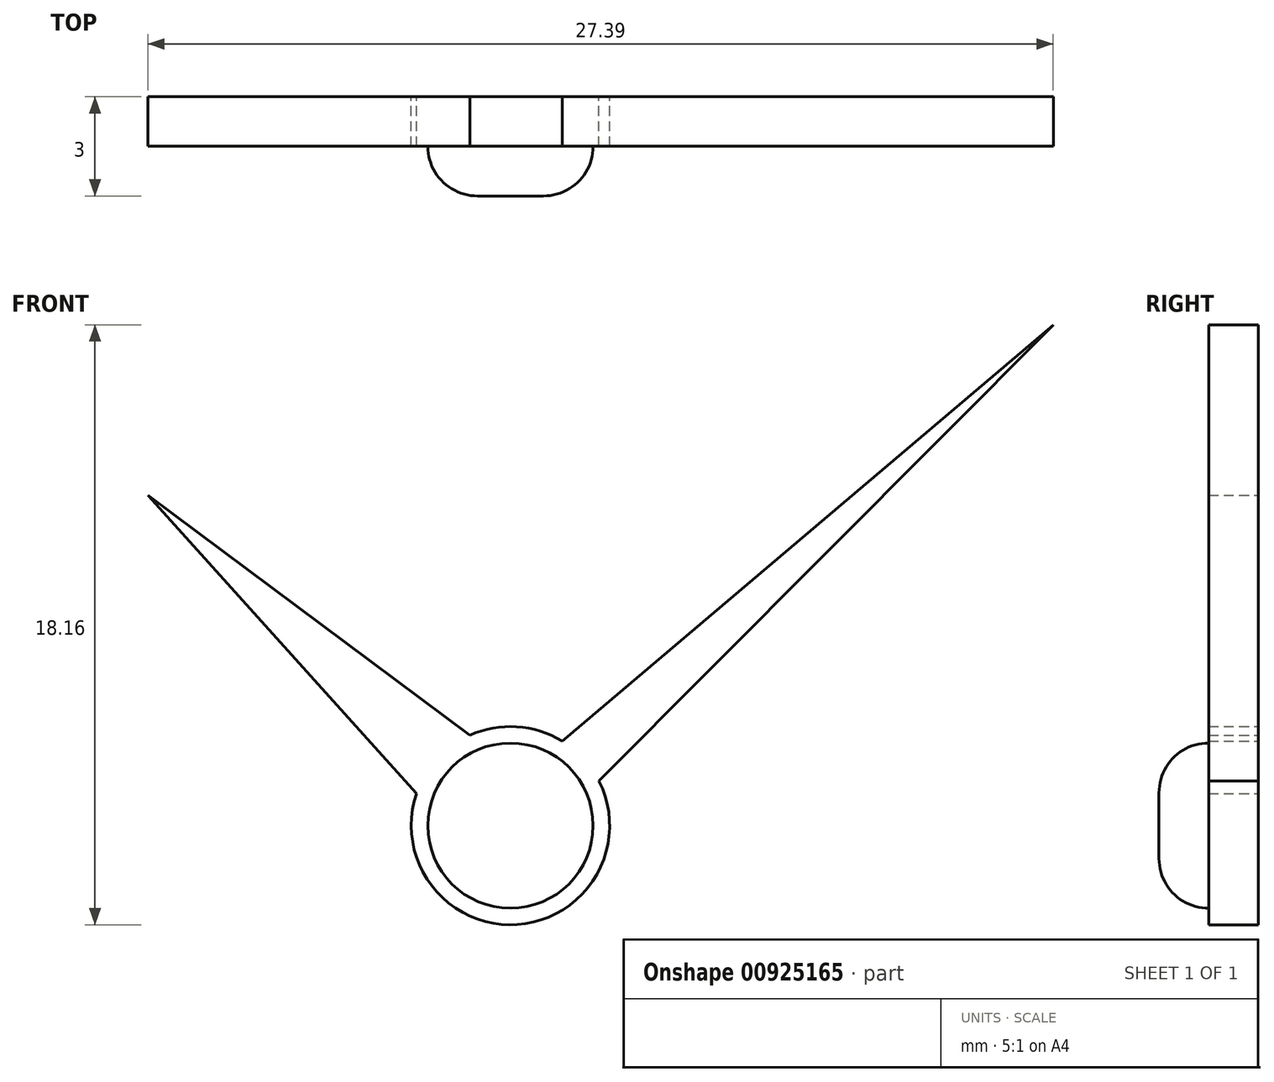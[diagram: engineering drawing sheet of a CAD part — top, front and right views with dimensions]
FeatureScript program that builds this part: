
annotation { "Feature Type Name" : "Feature", "Feature Type Description" : "" }
export const myFeature = defineFeature(function(context is Context, id is Id, definition is map)
    precondition{}
    {
        {
            var Q0;
            Q0=qCreatedBy(makeId("Front.planeOp"),FACE);
            var sketch = newSketch(context, id + "F0", { "sketchPlane" : qUnion([Q0])});
            skCircle(sketch, "E0", {"center": v(0, 0) * mm, "radius": 2.5 * mm});
            skSolve(sketch);
        }
        {
            var Q0;
            Q0 = qSketchRegion(id + "F0", true);
            extrude(context, id + "F1", {"entities" : qUnion([Q0]), "depth" : 3 * mm, "offsetDistance" : 25 * mm});
        }
        {
            var Q0;
            Q0=makeQuery(id+"F1.opExtrude","CAP_EDGE",EDGE,{"disambiguationData":[OSD([sQuery(id+"F0.wireOp",EDGE,"E0")])],"isStart":false});
            fillet(context, id + "F2", {"entities" : qUnion([Q0]), "radius" : 1.5 * mm, "tangentPropagation" : true, "allowEdgeOverflow" : false});
        }
        {
            var Q0;
            Q0=qCreatedBy(makeId("Front.planeOp"),FACE);
            var sketch = newSketch(context, id + "F3", { "sketchPlane" : qUnion([Q0])});
            skArc(sketch, "E1", {"start": v(-2.84, 0.97) * mm, "mid": v(0.2, -3) * mm, "end": v(2.68, 1.36) * mm});
            skLineSegment(sketch, "E2", {"start": v(0, 0) * mm, "end": v(22.1, 20.4) * mm, "construction": true});
            skLineSegment(sketch, "E3", {"start": v(0, 0) * mm, "end": v(-13.96, 12.72) * mm, "construction": true});
            skLineSegment(sketch, "E4", {"start": v(-10.97, 10) * mm, "end": v(-2.84, 0.97) * mm});
            skLineSegment(sketch, "E5.MirrorCS", {"start": v(-10.97, 10) * mm, "end": v(-1.23, 2.74) * mm});
            skLineSegment(sketch, "E6", {"start": v(1.57, 2.56) * mm, "end": v(16.42, 15.16) * mm});
            skLineSegment(sketch, "E7.MirrorCS", {"start": v(2.68, 1.36) * mm, "end": v(16.42, 15.16) * mm});
            skArc(sketch, "E8.trimOffspring", {"start": v(1.57, 2.56) * mm, "mid": v(0.19, 3) * mm, "end": v(-1.23, 2.74) * mm});
            skSolve(sketch);
        }
        {
            var Q0;
            Q0 = qSketchRegion(id + "F3", true);
            extrude(context, id + "F4", {"entities" : qUnion([Q0]), "operationType" : NewBodyOperationType.ADD, "depth" : 1.5 * mm, "offsetDistance" : 25 * mm});
        }
    });
